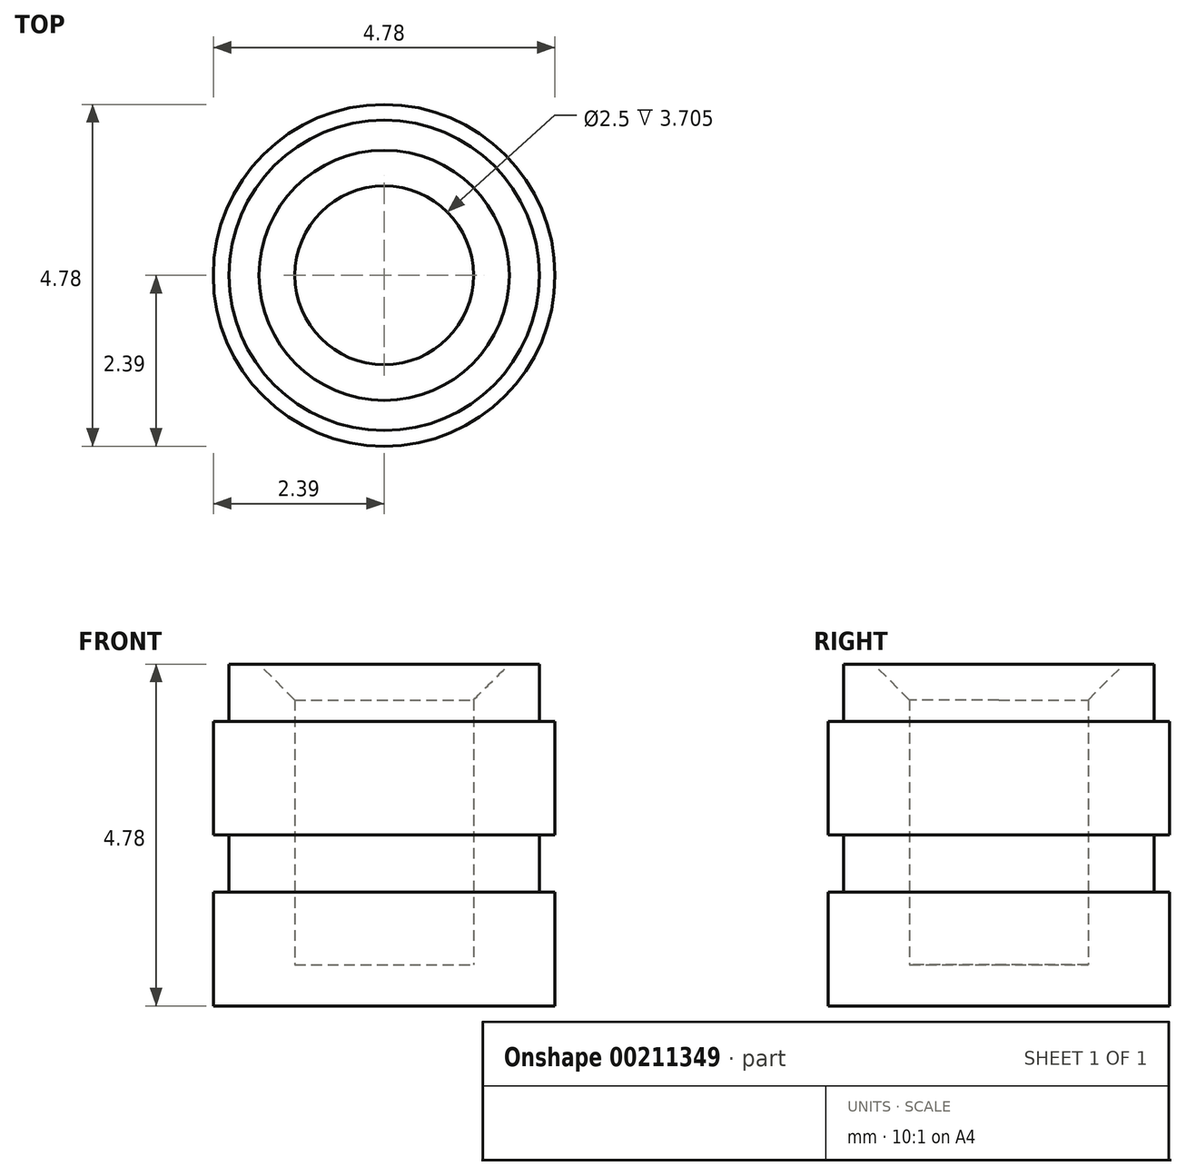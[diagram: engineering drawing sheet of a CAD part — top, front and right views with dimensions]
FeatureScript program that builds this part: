
annotation { "Feature Type Name" : "Feature", "Feature Type Description" : "" }
export const myFeature = defineFeature(function(context is Context, id is Id, definition is map)
    precondition{}
    {
        {
            var Q0;
            Q0=qCreatedBy(makeId("Front.planeOp"),FACE);
            var sketch = newSketch(context, id + "F0", { "sketchPlane" : qUnion([Q0])});
            skLineSegment(sketch, "E0", {"start": v(0, 0) * mm, "end": v(0, 4.78) * mm, "construction": true});
            skLineSegment(sketch, "E1", {"start": v(0, 0) * mm, "end": v(2.4, 0) * mm});
            skLineSegment(sketch, "E2", {"start": v(2.4, 0) * mm, "end": v(2.4, 1.6) * mm});
            skLineSegment(sketch, "E3", {"start": v(2.4, 1.6) * mm, "end": v(2.17, 1.6) * mm});
            skLineSegment(sketch, "E4", {"start": v(2.17, 1.6) * mm, "end": v(2.17, 2.4) * mm});
            skLineSegment(sketch, "E5", {"start": v(2.17, 2.4) * mm, "end": v(2.4, 2.4) * mm});
            skLineSegment(sketch, "E6", {"start": v(2.4, 2.4) * mm, "end": v(2.4, 3.98) * mm});
            skLineSegment(sketch, "E7", {"start": v(2.4, 3.98) * mm, "end": v(2.17, 3.98) * mm});
            skLineSegment(sketch, "E8", {"start": v(2.17, 3.98) * mm, "end": v(2.17, 4.78) * mm});
            skLineSegment(sketch, "E9", {"start": v(2.17, 4.78) * mm, "end": v(1.25, 4.78) * mm});
            skLineSegment(sketch, "E10", {"start": v(1.25, 4.78) * mm, "end": v(1.25, 0.58) * mm});
            skLineSegment(sketch, "E11", {"start": v(1.25, 0.58) * mm, "end": v(0, 0.58) * mm});
            skLineSegment(sketch, "E12", {"start": v(0, 0.58) * mm, "end": v(0, 0) * mm});
            skSolve(sketch);
        }
        {
            var Q0;
            Q0=qCreatedBy(makeId("Front.planeOp"),FACE);
            var sketch = newSketch(context, id + "F1", { "sketchPlane" : qUnion([Q0])});
            skLineSegment(sketch, "E13", {"start": v(0, 0) * mm, "end": v(0, 4.78) * mm, "construction": true});
            skLineSegment(sketch, "E14", {"start": v(0, 0) * mm, "end": v(2.88, 0) * mm});
            skLineSegment(sketch, "E15", {"start": v(2.88, 0) * mm, "end": v(2.88, 4.78) * mm});
            skSolve(sketch);
        }
        {
            var Q0;
            Q0 = qSketchRegion(id + "F0", true);
            var Q1;
            Q1=sQuery(id+"F1.wireOp",EDGE,"E13");
            revolve(context, id + "F2", {"entities" : qUnion([Q0]), "axis" : qUnion([Q1]), "revolveType" : RevolveType.FULL});
        }
        {
            var Q0;
            Q0=makeQuery(id+"F2.opRevolve","SWEPT_EDGE",EDGE,{"disambiguationData":[OSD([sQuery(id+"F0.wireOp",EDGE,"E9"),sQuery(id+"F0.wireOp",EDGE,"E10")])]});
            chamfer(context, id + "F3", {"entities" : qUnion([Q0]), "width" : .5 * mm, "tangentPropagation" : true});
        }
    });
